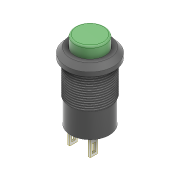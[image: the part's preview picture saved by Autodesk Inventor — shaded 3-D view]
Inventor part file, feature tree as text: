
AUTODESK INVENTOR PART (.ipt)
format: ipt  version: 2020 (Build 240168000, 168)  size: 620,032 bytes
history: native  units: mm
features: sketch x6, extrude x4, revolve x1, helix x1, chamfer x1, fillet x1
ambient origin geometry x8: Origin, YZ Plane, XZ Plane, XY Plane, X Axis, Y Axis, Z Axis, Center Point
bodies: Solid1 (feature_tree), Solid2 (feature_tree), Solid3 (feature_tree)
feature tree (14):
  revolve  "Revolution1"  [1 undecoded]
  helix  "Coil1"  [1 undecoded]
  extrude  "Extrusion1"  Depth=12.33mm
  extrude  "Extrusion2"  Depth=10.0mm
  extrude  "Extrusion3"  Depth=1.25mm
  chamfer  "Chamfer1"  Angle=90.0deg  [1 undecoded]
  extrude  "Extrusion4"  Depth=0.5mm
  fillet  "Fillet1"  Radius=0.31mm
  sketch  "Sketch1"  dims[d0=9.1mm d1=20.0mm d2=45.0deg]
  sketch  "Sketch2"  dims[d3=11.5mm d4=12.33mm]
  sketch  "Sketch3"  dims[d5=10.0mm d6=11.7mm]
  sketch  "Sketch4"  dims[d7=14.2mm d8=1.25mm]
  sketch  "Sketch5"  dims[d9=2.75mm]
  sketch  "Sketch6"  dims[d10=6.0mm d11=90.0deg d12=0.762mm d13=0.31mm d14=60.0deg d15=10.762mm d16=0.635mm d17=10.762mm d18=10.0mm d19=0.0mm d20=90.0deg d21=90.0deg d22=0.0mm d23=0.0mm d24=10.0mm d25=0.0mm d26=0.6mm d27=2.15mm d28=5.5mm d29=2.5mm d30=5.63mm d31=0.0mm d32=1.0mm d33=2.5mm d34=1.0mm d35=0.0mm d36=0.0mm d37=0.2mm d38=2.0mm d39=45.0deg d40=0.1mm d41=6.0mm d42=0.0mm d43=0.5mm]
note: 3 required parameter values undecoded (feature->parameter linkage not recoverable at this tier; creation-order binding heuristic only, values carry confidence <= 0.55)